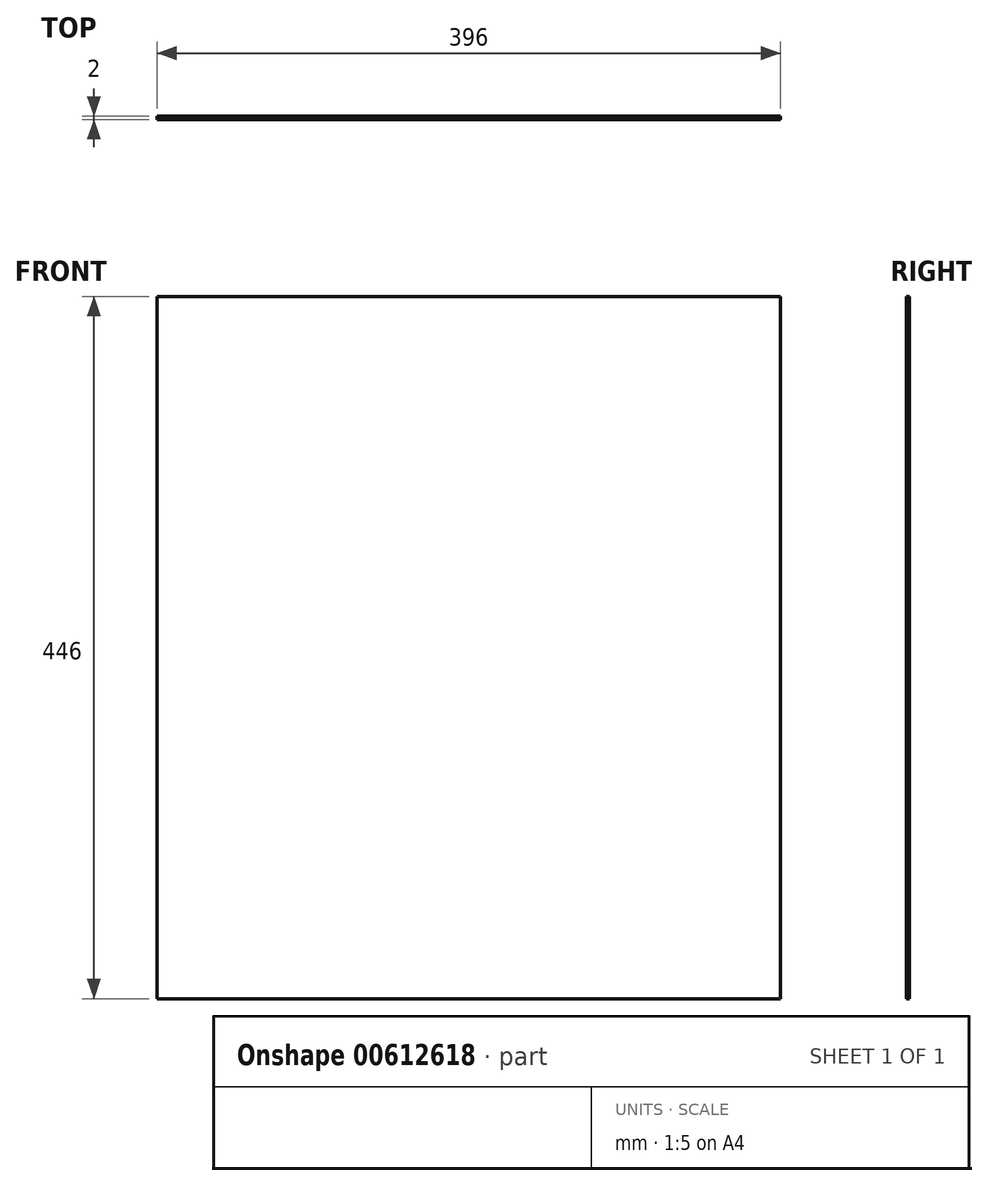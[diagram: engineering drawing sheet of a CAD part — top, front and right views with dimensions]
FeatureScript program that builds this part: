
annotation { "Feature Type Name" : "Feature", "Feature Type Description" : "" }
export const myFeature = defineFeature(function(context is Context, id is Id, definition is map)
    precondition{}
    {
        {
            var Q0;
            Q0=qCreatedBy(makeId("Front.planeOp"),FACE);
            var sketch = newSketch(context, id + "F0", { "sketchPlane" : qUnion([Q0])});
            skPoint(sketch, "E0.middle", {"position": v(0, 0) * mm});
            skLineSegment(sketch, "E1.bottom", {"start": v(-199, 296.75) * mm, "end": v(197, 296.75) * mm});
            skLineSegment(sketch, "E1.top", {"start": v(-199, -149.25) * mm, "end": v(197, -149.25) * mm});
            skLineSegment(sketch, "E1.left", {"start": v(-199, 296.75) * mm, "end": v(-199, -149.25) * mm});
            skLineSegment(sketch, "E1.right", {"start": v(197, 296.75) * mm, "end": v(197, -149.25) * mm});
            skSolve(sketch);
        }
        {
            var Q0;
            Q0=makeQuery(id+"F0.imprint","IMPRINT",FACE,{"disambiguationData":[TD([[makeQuery(id+"F0.imprint","IMPRINT",EDGE,{"derivedFrom":sQuery(id+"F0.wireOp",EDGE,"E1.bottom")}),-1.0]])]});
            extrude(context, id + "F1", {"entities" : qUnion([Q0]), "depth" : 2 * mm, "offsetDistance" : 25.4 * mm});
        }
    });
